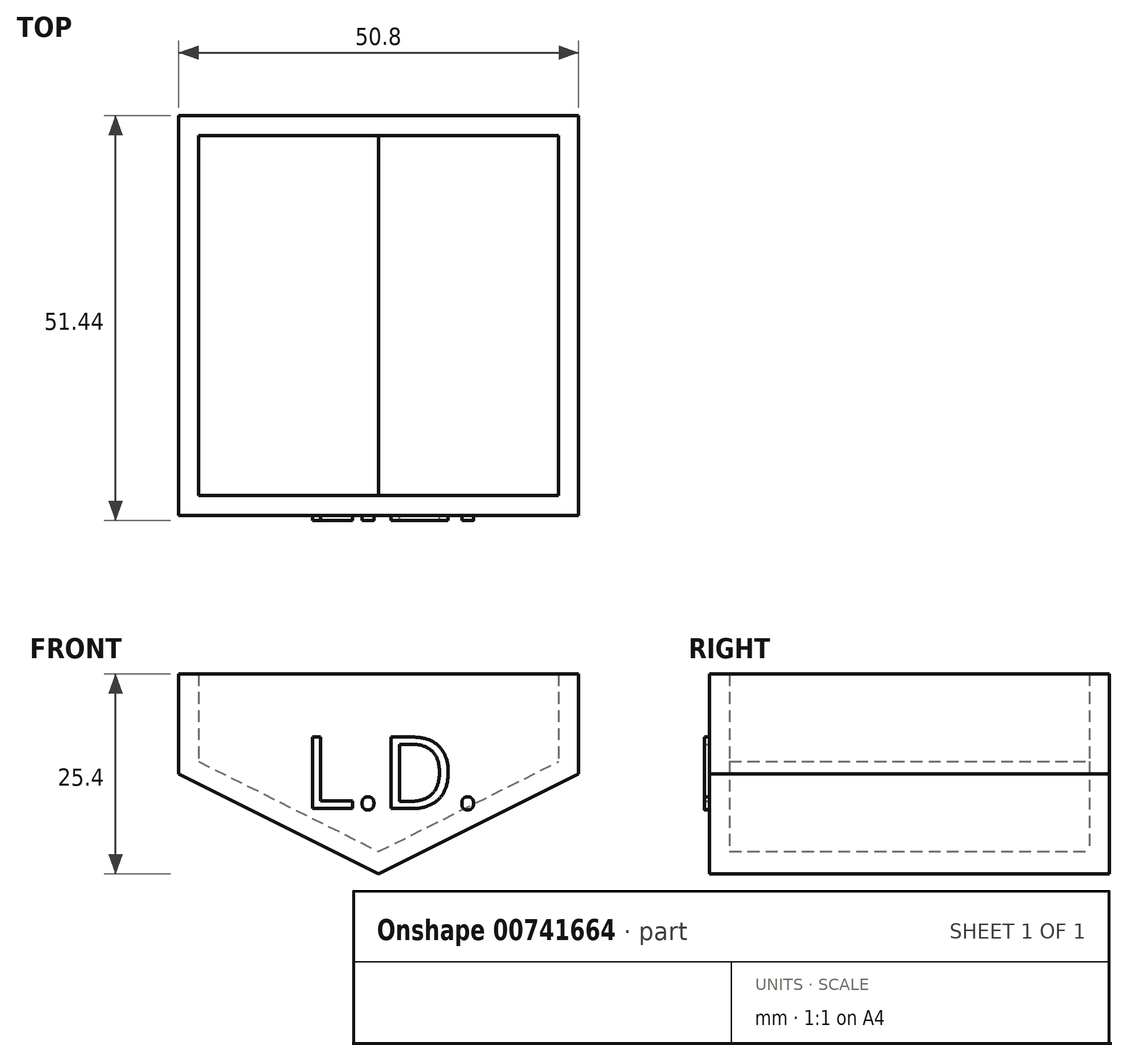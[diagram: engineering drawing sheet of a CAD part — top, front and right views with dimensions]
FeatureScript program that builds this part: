
annotation { "Feature Type Name" : "Feature", "Feature Type Description" : "" }
export const myFeature = defineFeature(function(context is Context, id is Id, definition is map)
    precondition{}
    {
        {
            var Q0;
            Q0=qCreatedBy(makeId("Front.planeOp"),FACE);
            var sketch = newSketch(context, id + "F0", { "sketchPlane" : qUnion([Q0])});
            skLineSegment(sketch, "E0", {"start": v(-42.16, 37.1) * mm, "end": v(8.64, 37.1) * mm});
            skLineSegment(sketch, "E1", {"start": v(-42.16, 37.1) * mm, "end": v(-42.16, 24.4) * mm});
            skLineSegment(sketch, "E2", {"start": v(8.64, 37.1) * mm, "end": v(8.64, 24.4) * mm});
            skLineSegment(sketch, "E3", {"start": v(-42.16, 24.4) * mm, "end": v(-16.76, 11.7) * mm});
            skLineSegment(sketch, "E4", {"start": v(-16.76, 11.7) * mm, "end": v(8.64, 24.4) * mm});
            skSolve(sketch);
        }
        {
            var Q0;
            Q0=makeQuery(id+"F0.imprint","IMPRINT",FACE,{"disambiguationData":[TD([[makeQuery(id+"F0.imprint","IMPRINT",EDGE,{"derivedFrom":sQuery(id+"F0.wireOp",EDGE,"E0")}),-1.0]])]});
            extrude(context, id + "F1", {"entities" : qUnion([Q0]), "depth" : 50.8 * mm, "offsetDistance" : 25.4 * mm});
        }
        {
            var Q0;
            Q0=makeQuery(id+"F1.opExtrude","SWEPT_FACE",FACE,{"disambiguationData":[OSD([sQuery(id+"F0.wireOp",EDGE,"E0")])]});
            shell(context, id + "F2", {"entities" : qUnion([Q0]), "thickness" : 2.54 * mm});
        }
        {
            var Q0;
            Q0=makeQuery(id+"F1.opExtrude","CAP_FACE",FACE,{"disambiguationData":[OSD([sQuery(id+"F0.wireOp",EDGE,"E0"),sQuery(id+"F0.wireOp",EDGE,"E1"),sQuery(id+"F0.wireOp",EDGE,"E2"),sQuery(id+"F0.wireOp",EDGE,"E3"),sQuery(id+"F0.wireOp",EDGE,"E4")])],"isStart":false});
            var sketch = newSketch(context, id + "F3", { "sketchPlane" : qUnion([Q0])});
            skText(sketch, "E5", { "text": "L.D.", "fontName": "OpenSans-Regular.ttf"});
            const initialGuessF3  = {"E5": [-0.02641, 0.02, 1, 0, 0.00916]};
            skSetInitialGuess(sketch, initialGuessF3);
            skSolve(sketch);
        }
        {
            var Q0;
            Q0 = qSketchRegion(id + "F3", true);
            extrude(context, id + "F4", {"entities" : qUnion([Q0]), "operationType" : NewBodyOperationType.ADD, "depth" : 0.64 * mm, "offsetDistance" : 25.4 * mm});
        }
    });
